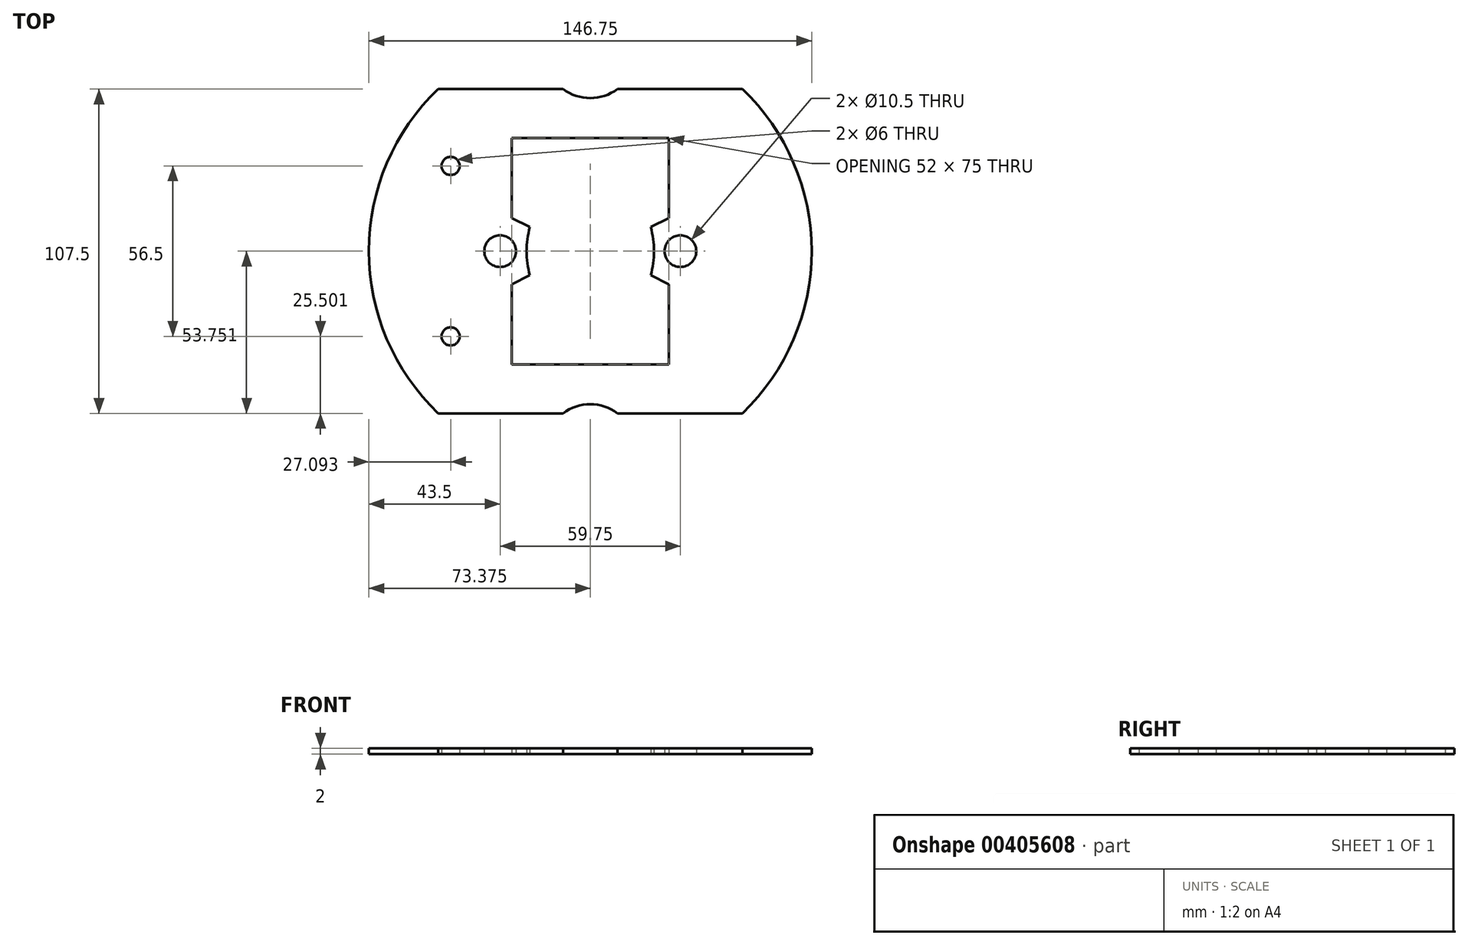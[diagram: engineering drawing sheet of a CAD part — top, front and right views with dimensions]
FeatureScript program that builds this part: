
annotation { "Feature Type Name" : "Feature", "Feature Type Description" : "" }
export const myFeature = defineFeature(function(context is Context, id is Id, definition is map)
    precondition{}
    {
        {
            var Q0;
            Q0=qCreatedBy(makeId("Top.planeOp"),FACE);
            var sketch = newSketch(context, id + "F0", { "sketchPlane" : qUnion([Q0])});
            skLineSegment(sketch, "E0.bottom", {"start": v(-148.37, 73.57) * mm, "end": v(-107, 73.57) * mm});
            skLineSegment(sketch, "E0.top", {"start": v(-148.37, -33.93) * mm, "end": v(-107, -33.93) * mm});
            skLineSegment(sketch, "E1", {"start": v(-171.37, 19.82) * mm, "end": v(-24.62, 19.82) * mm, "construction": true});
            skLineSegment(sketch, "E2", {"start": v(-98, 73.57) * mm, "end": v(-98, -33.93) * mm, "construction": true});
            skLineSegment(sketch, "E3", {"start": v(-148.37, 73.57) * mm, "end": v(-148.37, -33.93) * mm, "construction": true});
            skLineSegment(sketch, "E4", {"start": v(-47.62, 73.57) * mm, "end": v(-47.62, -33.93) * mm, "construction": true});
            skArc(sketch, "E5", {"start": v(-47.62, -33.93) * mm, "mid": v(-24.62, 19.82) * mm, "end": v(-47.62, 73.57) * mm});
            skArc(sketch, "E6", {"start": v(-148.37, 73.57) * mm, "mid": v(-171.37, 19.82) * mm, "end": v(-148.37, -33.93) * mm});
            skPoint(sketch, "E7.orphan", {"position": v(-171.37, 73.57) * mm});
            skPoint(sketch, "E8.orphan", {"position": v(-171.37, -33.93) * mm});
            skPoint(sketch, "E9.orphan", {"position": v(-24.62, -33.93) * mm});
            skPoint(sketch, "E10.orphan", {"position": v(-24.62, 73.57) * mm});
            skLineSegment(sketch, "E11", {"start": v(-153.14, 68.57) * mm, "end": v(-42.85, 68.57) * mm, "construction": true});
            skLineSegment(sketch, "E12", {"start": v(-153.14, -28.93) * mm, "end": v(-42.85, -28.93) * mm, "construction": true});
            skLineSegment(sketch, "E13", {"start": v(-107, 73.57) * mm, "end": v(-107, -33.93) * mm, "construction": true});
            skLineSegment(sketch, "E14", {"start": v(-89, -33.93) * mm, "end": v(-89, 73.57) * mm, "construction": true});
            skArc(sketch, "E15", {"start": v(-107, 73.57) * mm, "mid": v(-98, 70.57) * mm, "end": v(-89, 73.57) * mm});
            skArc(sketch, "E16", {"start": v(-89, -33.93) * mm, "mid": v(-98, -30.93) * mm, "end": v(-107, -33.93) * mm});
            skLineSegment(sketch, "E17.trimOffspring", {"start": v(-89, -33.93) * mm, "end": v(-47.62, -33.93) * mm});
            skLineSegment(sketch, "E18.trimOffspring", {"start": v(-89, 73.57) * mm, "end": v(-47.62, 73.57) * mm});
            skCircle(sketch, "E19", {"center": v(-68.12, 19.82) * mm, "radius": 5.25 * mm});
            skCircle(sketch, "E20.MirrorC", {"center": v(-127.87, 19.82) * mm, "radius": 5.25 * mm});
            skCircle(sketch, "E21", {"center": v(-144.28, 48.07) * mm, "radius": 3 * mm});
            skCircle(sketch, "E22.MirrorC", {"center": v(-144.28, -8.43) * mm, "radius": 3 * mm});
            skLineSegment(sketch, "E23.bottom", {"start": v(-124, 57.32) * mm, "end": v(-72, 57.32) * mm});
            skLineSegment(sketch, "E23.top", {"start": v(-124, -17.68) * mm, "end": v(-72, -17.68) * mm});
            skLineSegment(sketch, "E23.left", {"start": v(-124, 57.32) * mm, "end": v(-124, 30.82) * mm});
            skLineSegment(sketch, "E23.right", {"start": v(-72, 57.32) * mm, "end": v(-72, 30.82) * mm});
            skLineSegment(sketch, "E24", {"start": v(-124, 30.82) * mm, "end": v(-107, 30.82) * mm, "construction": true});
            skLineSegment(sketch, "E25", {"start": v(-124, 27.82) * mm, "end": v(-107, 27.82) * mm, "construction": true});
            skLineSegment(sketch, "E26", {"start": v(-119.12, 19.82) * mm, "end": v(-119.12, 27.82) * mm, "construction": true});
            skLineSegment(sketch, "E27", {"start": v(-124, 30.82) * mm, "end": v(-118, 27.82) * mm});
            skArc(sketch, "E28", {"start": v(-118, 27.82) * mm, "mid": v(-118.84, 23.86) * mm, "end": v(-119.12, 19.82) * mm});
            skArc(sketch, "E29.MirrorCS", {"start": v(-118, 11.82) * mm, "mid": v(-118.84, 15.78) * mm, "end": v(-119.12, 19.82) * mm});
            skLineSegment(sketch, "E30.MirrorCS", {"start": v(-124, 8.82) * mm, "end": v(-118, 11.82) * mm});
            skLineSegment(sketch, "E31.MirrorCS", {"start": v(-72, 30.82) * mm, "end": v(-77.98, 27.82) * mm});
            skArc(sketch, "E32.MirrorCS", {"start": v(-77.98, 27.82) * mm, "mid": v(-77.15, 23.86) * mm, "end": v(-76.87, 19.82) * mm});
            skArc(sketch, "E33.MirrorCS", {"start": v(-77.98, 11.82) * mm, "mid": v(-77.15, 15.78) * mm, "end": v(-76.87, 19.82) * mm});
            skLineSegment(sketch, "E34.MirrorCS", {"start": v(-72, 8.82) * mm, "end": v(-77.98, 11.82) * mm});
            skLineSegment(sketch, "E35.trimOffspring", {"start": v(-124, 8.82) * mm, "end": v(-124, -17.68) * mm});
            skLineSegment(sketch, "E36.trimOffspring", {"start": v(-72, 8.82) * mm, "end": v(-72, -17.68) * mm});
            skSolve(sketch);
        }
        {
            var Q0;
            Q0 = qSketchRegion(id + "F0", true);
            extrude(context, id + "F1", {"entities" : qUnion([Q0]), "depth" : 2 * mm});
        }
    });
